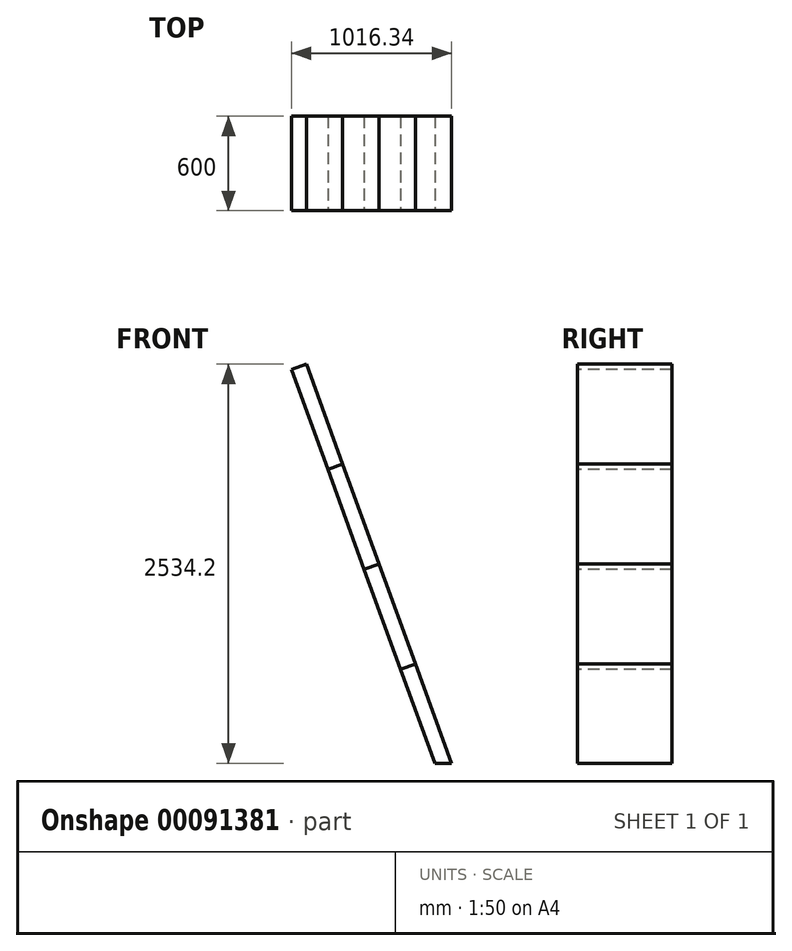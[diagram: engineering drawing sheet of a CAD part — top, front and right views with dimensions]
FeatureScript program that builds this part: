
annotation { "Feature Type Name" : "Feature", "Feature Type Description" : "" }
export const myFeature = defineFeature(function(context is Context, id is Id, definition is map)
    precondition{}
    {
        {
            var Q0;
            Q0=qCreatedBy(makeId("Front.planeOp"),FACE);
            var sketch = newSketch(context, id + "F0", { "sketchPlane" : qUnion([Q0])});
            skLineSegment(sketch, "E0", {"start": v(0, 0) * mm, "end": v(0, 2500) * mm, "construction": true});
            skLineSegment(sketch, "E1", {"start": v(0, 0) * mm, "end": v(2000, 0) * mm, "construction": true});
            skLineSegment(sketch, "E2", {"start": v(0, 2500) * mm, "end": v(669.87, 0) * mm, "construction": true});
            skLineSegment(sketch, "E3", {"start": v(0, 2500) * mm, "end": v(1165.77, 0) * mm, "construction": true});
            skLineSegment(sketch, "E4", {"start": v(0, 2500) * mm, "end": v(93.97, 2534.2) * mm});
            skLineSegment(sketch, "E5", {"start": v(93.97, 2534.2) * mm, "end": v(324.83, 1899.9) * mm});
            skLineSegment(sketch, "E6", {"start": v(1016.34, 0) * mm, "end": v(909.93, 0) * mm});
            skLineSegment(sketch, "E7", {"start": v(324.83, 1899.9) * mm, "end": v(555.7, 1265.62) * mm});
            skLineSegment(sketch, "E8", {"start": v(555.7, 1265.62) * mm, "end": v(786.56, 631.32) * mm});
            skLineSegment(sketch, "E9", {"start": v(786.56, 631.32) * mm, "end": v(1016.34, 0) * mm});
            skLineSegment(sketch, "E10", {"start": v(0, 2500) * mm, "end": v(909.93, 0) * mm});
            skLineSegment(sketch, "E11", {"start": v(324.83, 1899.9) * mm, "end": v(230.86, 1865.7) * mm});
            skLineSegment(sketch, "E12", {"start": v(555.7, 1265.62) * mm, "end": v(461.73, 1231.41) * mm});
            skLineSegment(sketch, "E13", {"start": v(786.56, 631.32) * mm, "end": v(692.6, 597.12) * mm});
            skLineSegment(sketch, "E14", {"start": v(375.88, 2636.8) * mm, "end": v(1335.6, 0) * mm, "construction": true});
            skLineSegment(sketch, "E15", {"start": v(324.83, 1899.9) * mm, "end": v(606.74, 2002.52) * mm, "construction": true});
            skArc(sketch, "E16", {"start": v(606.74, 2002.52) * mm, "mid": v(453.68, 1859.84) * mm, "end": v(268.36, 1762.7) * mm, "construction": true});
            skLineSegment(sketch, "E17", {"start": v(187.94, 2568.4) * mm, "end": v(418.8, 1934.11) * mm, "construction": true});
            skLineSegment(sketch, "E18", {"start": v(281.9, 2602.6) * mm, "end": v(512.77, 1968.31) * mm, "construction": true});
            skLineSegment(sketch, "E19", {"start": v(93.97, 2534.2) * mm, "end": v(187.94, 2568.4) * mm, "construction": true});
            skLineSegment(sketch, "E20", {"start": v(187.94, 2568.4) * mm, "end": v(281.9, 2602.6) * mm, "construction": true});
            skLineSegment(sketch, "E21", {"start": v(281.9, 2602.6) * mm, "end": v(375.88, 2636.8) * mm, "construction": true});
            skArc(sketch, "E22", {"start": v(281.9, 2602.6) * mm, "mid": v(807.23, 2412.67) * mm, "end": v(1028.84, 1899.9) * mm, "construction": true});
            skLineSegment(sketch, "E23", {"start": v(0, 2500) * mm, "end": v(800, 2500) * mm, "construction": true});
            skSolve(sketch);
        }
        {
            var Q0;
            {var subQ0=sQuery(id+"F0.wireOp",EDGE,"E4");Q0=makeQuery(id+"F0.imprint","IMPRINT",FACE,{"disambiguationData":[TD([[makeQuery(id+"F0.imprint","IMPRINT",EDGE,{"derivedFrom":subQ0}),-1.0]])]});}
            var Q1;
            Q1=makeQuery(id+"F0.imprint","IMPRINT",FACE,{"disambiguationData":[TD([[makeQuery(id+"F0.imprint","IMPRINT",EDGE,{"derivedFrom":sQuery(id+"F0.wireOp",EDGE,"E8")}),-1.0]])]});
            extrude(context, id + "F1", {"entities" : qUnion([Q0, Q1]), "oppositeDirection" : true, "depth" : 600 * mm});
        }
        {
            var Q0;
            Q0=makeQuery(id+"F0.imprint","IMPRINT",FACE,{"disambiguationData":[TD([[makeQuery(id+"F0.imprint","IMPRINT",EDGE,{"derivedFrom":sQuery(id+"F0.wireOp",EDGE,"E7")}),-1.0]])]});
            var Q1;
            {var subQ0=sQuery(id+"F0.wireOp",EDGE,"E6");Q1=makeQuery(id+"F0.imprint","IMPRINT",FACE,{"disambiguationData":[TD([[makeQuery(id+"F0.imprint","IMPRINT",EDGE,{"derivedFrom":subQ0}),-1.0]])]});}
            extrude(context, id + "F2", {"entities" : qUnion([Q0, Q1]), "oppositeDirection" : true, "depth" : 600 * mm});
        }
    });
